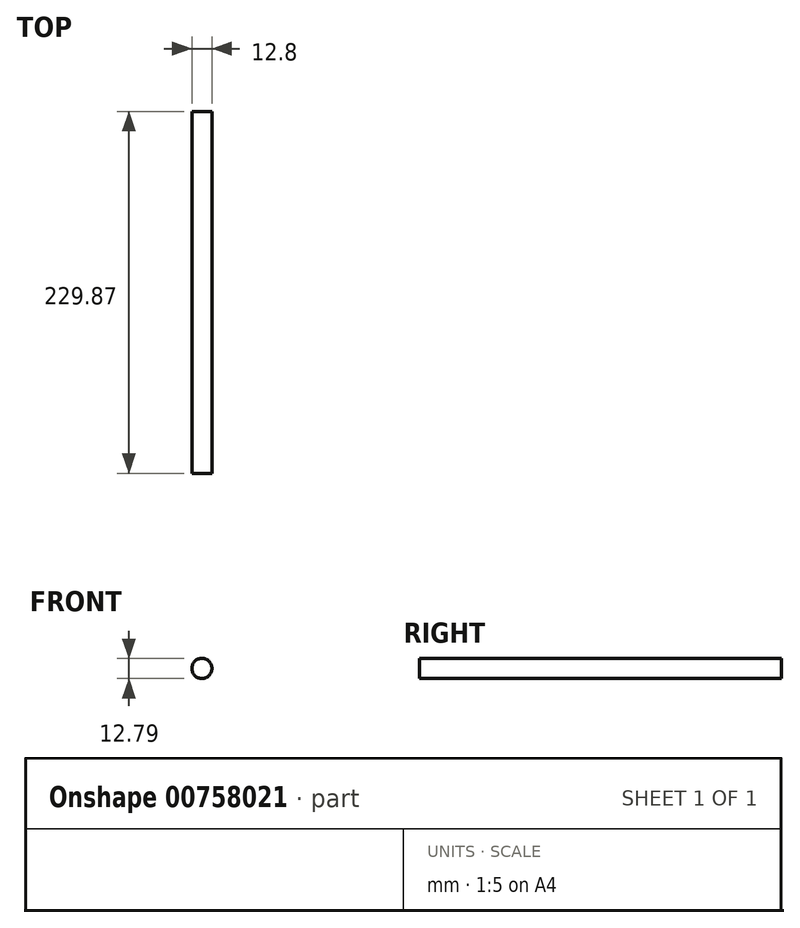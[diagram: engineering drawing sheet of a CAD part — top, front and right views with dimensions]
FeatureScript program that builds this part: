
annotation { "Feature Type Name" : "Feature", "Feature Type Description" : "" }
export const myFeature = defineFeature(function(context is Context, id is Id, definition is map)
    precondition{}
    {
        {
            var Q0;
            Q0=qCreatedBy(makeId("Front.planeOp"),FACE);
            var sketch = newSketch(context, id + "F0", { "sketchPlane" : qUnion([Q0])});
            skCircle(sketch, "E0", {"center": v(0, 35.7) * mm, "radius": 6.4 * mm});
            skSolve(sketch);
        }
        {
            var Q0;
            Q0=makeQuery(id+"F0.imprint","IMPRINT",FACE,{"disambiguationData":[TD([[makeQuery(id+"F0.imprint","IMPRINT",EDGE,{"derivedFrom":sQuery(id+"F0.wireOp",EDGE,"E0")}),1.0]])]});
            extrude(context, id + "F1", {"entities" : qUnion([Q0]), "depth" : 229.87 * mm, "offsetDistance" : 25.4 * mm});
        }
    });
